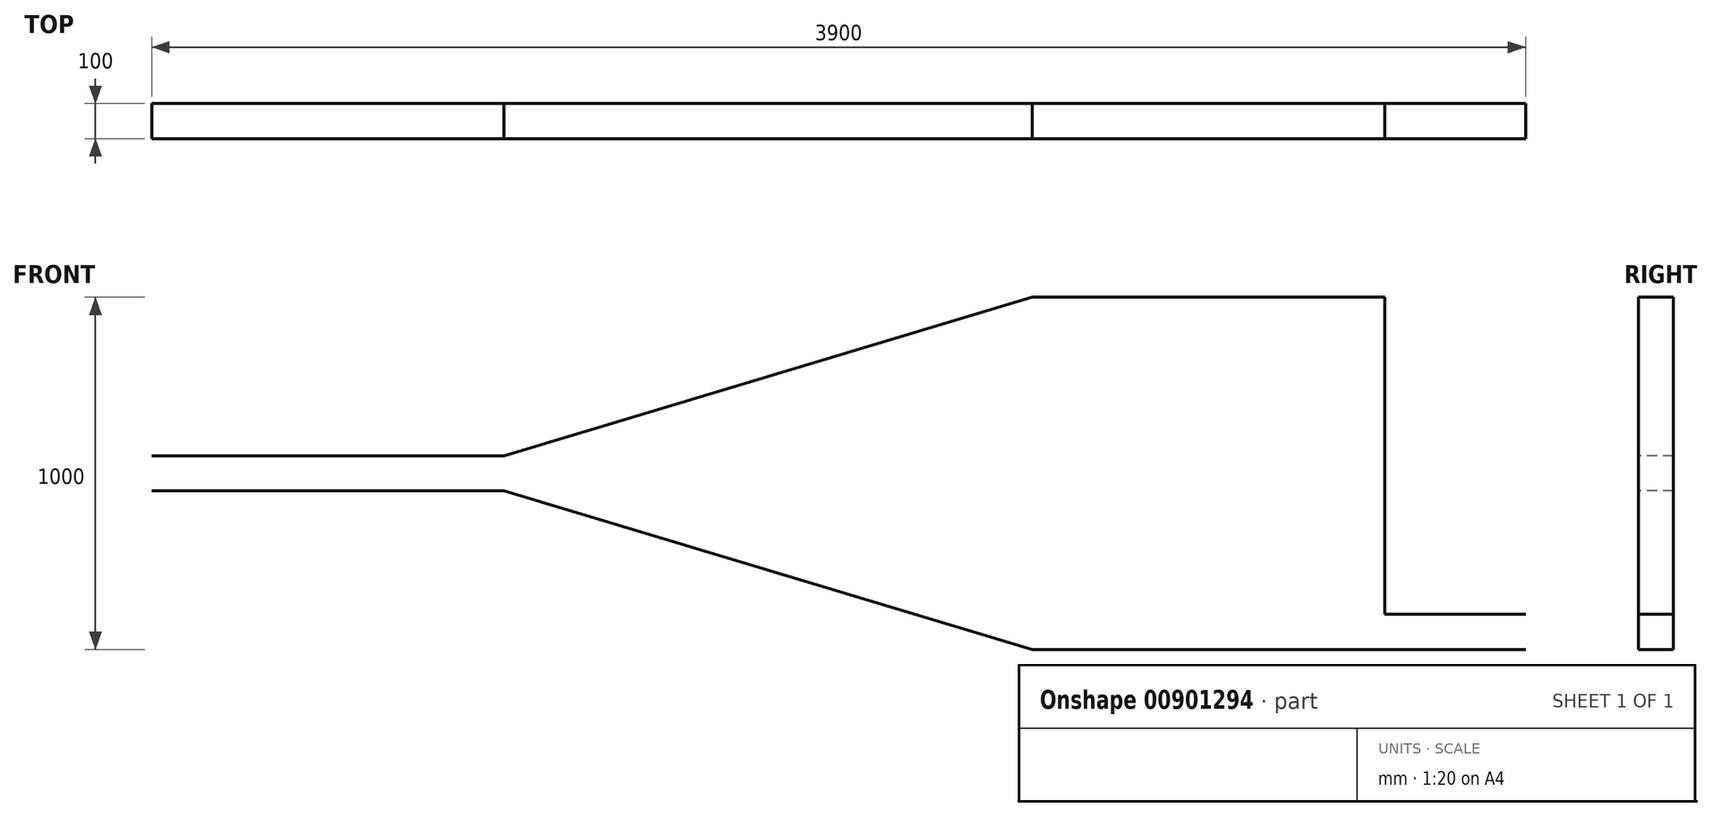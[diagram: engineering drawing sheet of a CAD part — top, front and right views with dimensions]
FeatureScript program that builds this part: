
annotation { "Feature Type Name" : "Feature", "Feature Type Description" : "" }
export const myFeature = defineFeature(function(context is Context, id is Id, definition is map)
    precondition{}
    {
        {
            var Q0;
            Q0=qCreatedBy(makeId("Front.planeOp"),FACE);
            var sketch = newSketch(context, id + "F0", { "sketchPlane" : qUnion([Q0])});
            skLineSegment(sketch, "E0.bottom", {"start": v(-1000, 50) * mm, "end": v(0, 50) * mm});
            skLineSegment(sketch, "E0.top", {"start": v(-1000, -50) * mm, "end": v(0, -50) * mm});
            skLineSegment(sketch, "E0.left", {"start": v(-1000, 50) * mm, "end": v(-1000, -50) * mm});
            skLineSegment(sketch, "E0.right", {"start": v(0, 50) * mm, "end": v(0, -50) * mm});
            skLineSegment(sketch, "E1.bottom", {"start": v(1500, 500) * mm, "end": v(2500, 500) * mm});
            skLineSegment(sketch, "E1.top", {"start": v(1500, -500) * mm, "end": v(2500, -500) * mm});
            skLineSegment(sketch, "E1.left", {"start": v(1500, 500) * mm, "end": v(1500, -500) * mm});
            skPoint(sketch, "E2", {"position": v(0, 0) * mm});
            skPoint(sketch, "E3", {"position": v(1500, 0) * mm});
            skLineSegment(sketch, "E4", {"start": v(0, 0) * mm, "end": v(1500, 0) * mm});
            skLineSegment(sketch, "E5", {"start": v(0, -50) * mm, "end": v(1500, -500) * mm});
            skLineSegment(sketch, "E6", {"start": v(0, 50) * mm, "end": v(1500, 500) * mm});
            skLineSegment(sketch, "E7", {"start": v(2500, -500) * mm, "end": v(2500, -400) * mm});
            skLineSegment(sketch, "E8", {"start": v(2500, -400) * mm, "end": v(2900, -400) * mm});
            skLineSegment(sketch, "E9", {"start": v(2900, -400) * mm, "end": v(2900, -500) * mm});
            skLineSegment(sketch, "E10", {"start": v(2900, -500) * mm, "end": v(2500, -500) * mm});
            skLineSegment(sketch, "E11", {"start": v(2500, 500) * mm, "end": v(2500, -400) * mm});
            skSolve(sketch);
        }
        {
            var Q0;
            Q0=sQuery(id+"F0.wireOp",EDGE,"E0.bottom");
            var Q1;
            Q1=sQuery(id+"F0.wireOp",EDGE,"E0.top");
            var Q2;
            Q2=sQuery(id+"F0.wireOp",EDGE,"E5");
            var Q3;
            Q3=sQuery(id+"F0.wireOp",EDGE,"E6");
            var Q4;
            Q4=sQuery(id+"F0.wireOp",EDGE,"E1.bottom");
            var Q5;
            Q5=sQuery(id+"F0.wireOp",EDGE,"E1.top");
            var Q6;
            Q6=sQuery(id+"F0.wireOp",EDGE,"E8");
            var Q7;
            Q7=sQuery(id+"F0.wireOp",EDGE,"E11");
            var Q8;
            Q8=sQuery(id+"F0.wireOp",EDGE,"E10");
            extrude(context, id + "F1", {"bodyType" : ToolBodyType.SURFACE, "surfaceEntities" : qUnion([Q0, Q1, Q2, Q3, Q4, Q5, Q6, Q7, Q8]), "depth" : 100 * mm, "offsetDistance" : 25 * mm});
        }
    });
